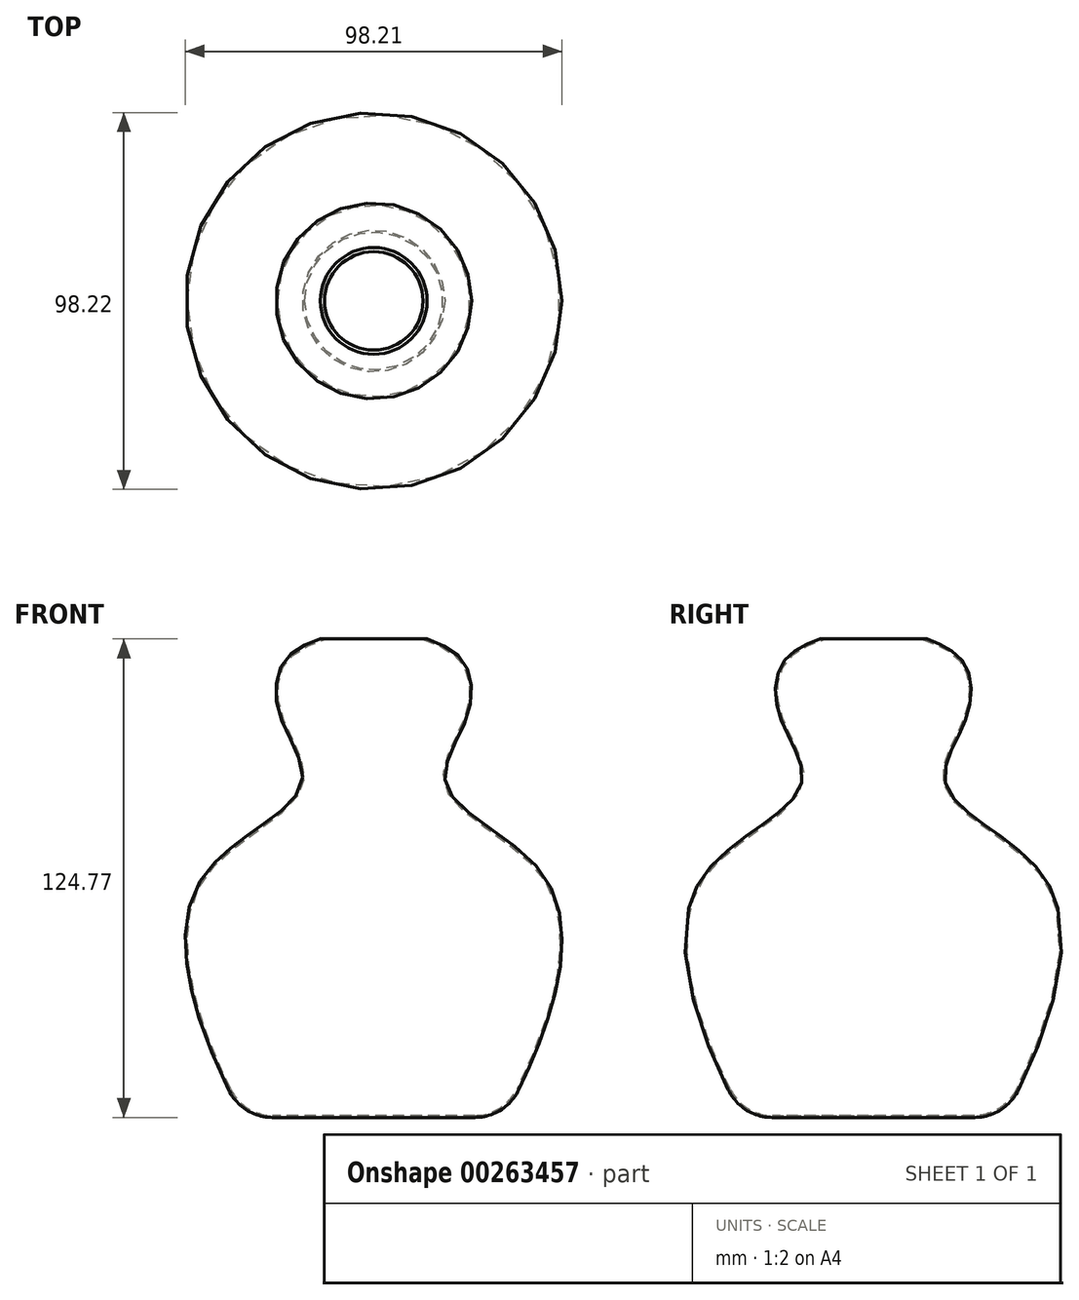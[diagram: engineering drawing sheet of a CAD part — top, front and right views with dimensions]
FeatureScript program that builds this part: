
annotation { "Feature Type Name" : "Feature", "Feature Type Description" : "" }
export const myFeature = defineFeature(function(context is Context, id is Id, definition is map)
    precondition{}
    {
        {
            var Q0;
            Q0=qCreatedBy(makeId("Front.planeOp"),FACE);
            var sketch = newSketch(context, id + "F0", { "sketchPlane" : qUnion([Q0])});
            skLineSegment(sketch, "E0", {"start": v(0, -75.85) * mm, "end": v(-26.36, -75.85) * mm});
            skFitSpline(sketch, "E1", {"points": [v(-34.25, -75.85) * mm, v(-46.73, -45.7) * mm, v(-43.9, -12.27) * mm, v(-18.95, 10.57) * mm, v(-24.36, 28.7) * mm, v(-22.95, 43.54) * mm, v(-8.35, 50.6) * mm], "startDerivative": vector(-73.8, 148.03) * mm, "endDerivative": vector(127.13, 36.07) * mm});
            skLineSegment(sketch, "E2", {"start": v(0, 50.6) * mm, "end": v(0, -75.85) * mm});
            skArc(sketch, "E3.filletArc", {"start": v(-37.8, -68.66) * mm, "mid": v(-33.11, -73.9) * mm, "end": v(-26.36, -75.85) * mm});
            skPoint(sketch, "E4.orphan", {"position": v(0, 58.13) * mm});
            skFitSpline(sketch, "E5", {"points": [v(-14.13, 48.96) * mm, v(0, 46.67) * mm], "startDerivative": vector(14.13, -2.3) * mm, "endDerivative": vector(14.13, -2.3) * mm});
            skSolve(sketch);
        }
        {
            var Q0;
            Q0=makeQuery(id+"F0.imprint","IMPRINT",FACE,{"disambiguationData":[TD([[makeQuery(id+"F0.imprint","IMPRINT",EDGE,{"derivedFrom":sQuery(id+"F0.wireOp",EDGE,"E0")}),-1.0]])]});
            var Q1;
            Q1=sQuery(id+"F0.wireOp",EDGE,"E2");
            revolve(context, id + "F1", {"entities" : qUnion([Q0]), "axis" : qUnion([Q1]), "revolveType" : RevolveType.FULL});
        }
        {
            var Q0;
            Q0=makeQuery(id+"F1.opRevolve","SWEPT_FACE",FACE,{"disambiguationData":[OSD([sQuery(id+"F0.wireOp",EDGE,"E5")])]});
            shell(context, id + "F2", {"entities" : qUnion([Q0]), "thickness" : 0.5 * mm});
        }
    });
